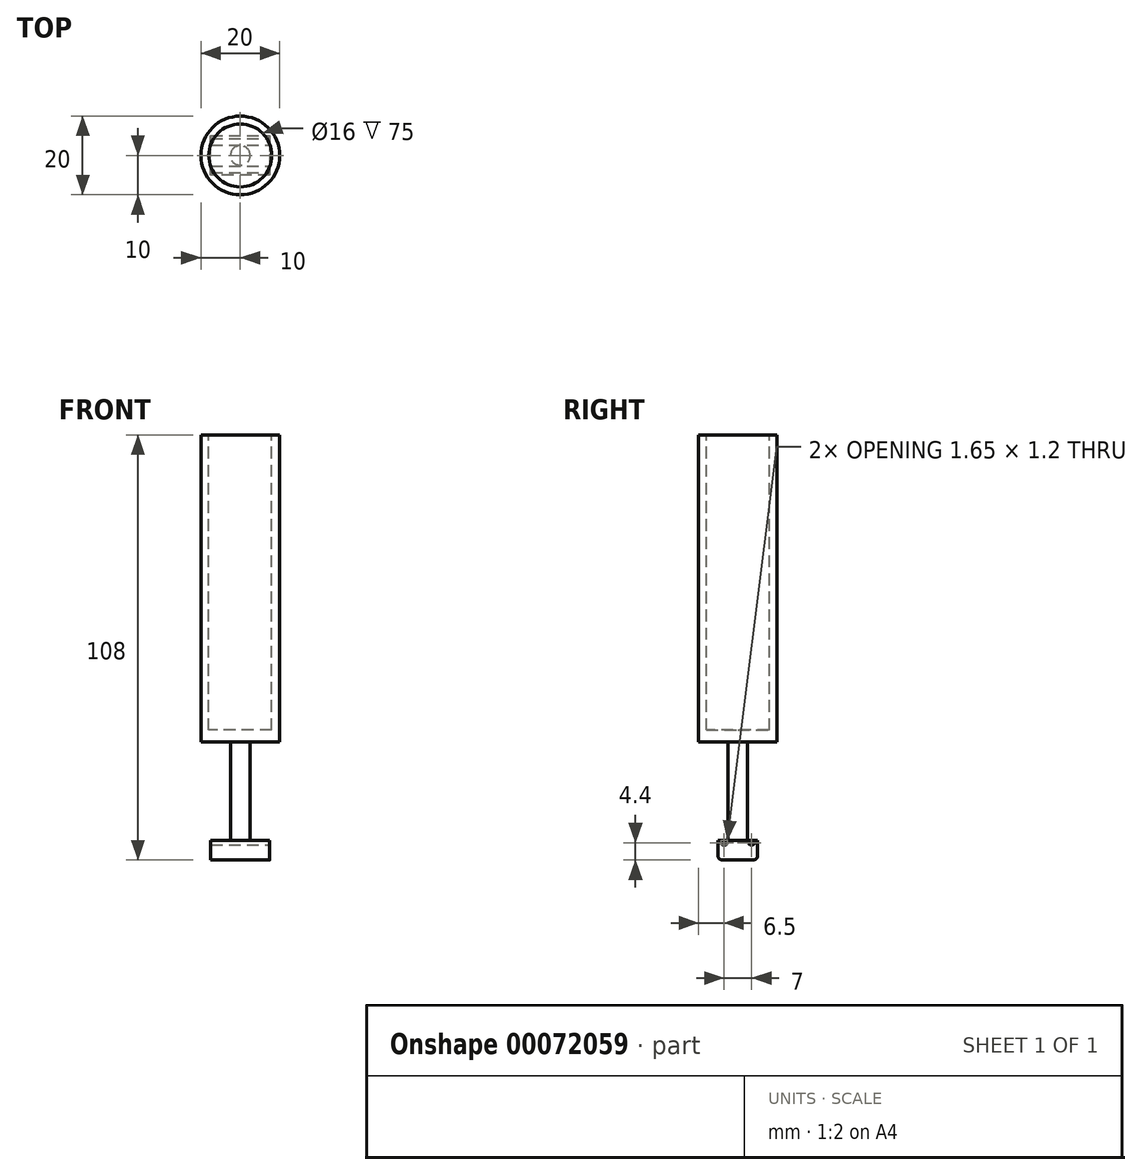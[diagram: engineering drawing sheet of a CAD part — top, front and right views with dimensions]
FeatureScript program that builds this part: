
annotation { "Feature Type Name" : "Feature", "Feature Type Description" : "" }
export const myFeature = defineFeature(function(context is Context, id is Id, definition is map)
    precondition{}
    {
        {
            var Q0;
            Q0=qCreatedBy(makeId("Top.planeOp"),FACE);
            var sketch = newSketch(context, id + "F0", { "sketchPlane" : qUnion([Q0])});
            skLineSegment(sketch, "E0", {"start": v(0, 10) * mm, "end": v(15, 10) * mm});
            skLineSegment(sketch, "E1", {"start": v(15, 10) * mm, "end": v(15, 0) * mm});
            skLineSegment(sketch, "E2", {"start": v(15, 0) * mm, "end": v(0, 0) * mm});
            skLineSegment(sketch, "E3", {"start": v(0, 0) * mm, "end": v(0, 10) * mm});
            skSolve(sketch);
        }
        {
            var Q0;
            Q0=qSketchRegion(id+"F0",true);
            extrude(context, id + "F1", {"entities" : qUnion([Q0]), "depth" : 5 * mm});
        }
        {
            var Q0;
            Q0=makeQuery(id+"F1.opExtrude","CAP_FACE",FACE,{"disambiguationData":[OSD([sQuery(id+"F0.wireOp",EDGE,"E0"),sQuery(id+"F0.wireOp",EDGE,"E1"),sQuery(id+"F0.wireOp",EDGE,"E2"),sQuery(id+"F0.wireOp",EDGE,"E3")])],"isStart":false});
            var sketch = newSketch(context, id + "F2", { "sketchPlane" : qUnion([Q0])});
            skLineSegment(sketch, "E4", {"start": v(0, 5) * mm, "end": v(15, 5) * mm, "construction": true});
            skLineSegment(sketch, "E5", {"start": v(7.5, 10) * mm, "end": v(7.5, 0) * mm, "construction": true});
            skCircle(sketch, "E6", {"center": v(7.5, 5) * mm, "radius": 2.5 * mm});
            skSolve(sketch);
        }
        {
            var Q0;
            Q0=makeQuery(id+"F2.imprint","IMPRINT",FACE,{"disambiguationData":[TD([[makeQuery(id+"F2.imprint","IMPRINT",EDGE,{"derivedFrom":sQuery(id+"F2.wireOp",EDGE,"E6")}),1.0]])]});
            var Q1;
            Q1=sQuery(id+"F2.wireOp",EDGE,"E6");
            extrude(context, id + "F3", {"entities" : qUnion([Q0]), "operationType" : NewBodyOperationType.ADD, "surfaceEntities" : qUnion([Q1]), "depth" : 100 * mm});
        }
        {
            var Q0;
            Q0=qCreatedBy(makeId("Top.planeOp"),FACE);
            cPlane(context, id + "F4", {"entities" : qUnion([Q0]), "cplaneType" : CPlaneType.OFFSET, "offset" : 30 * mm, "width" : 150 * mm, "height" : 150 * mm});
        }
        {
            var Q0;
            Q0=qCreatedBy(id+"F4.planeOp",FACE);
            var sketch = newSketch(context, id + "F5", { "sketchPlane" : qUnion([Q0])});
            skCircle(sketch, "E7", {"center": v(7.5, 5) * mm, "radius": 10 * mm});
            skSolve(sketch);
        }
        {
            var Q0;
            Q0=makeQuery(id+"F1.opExtrude","CAP_EDGE",EDGE,{"disambiguationData":[OSD([sQuery(id+"F0.wireOp",EDGE,"E2")])],"isStart":true});
            var Q1;
            Q1=makeQuery(id+"F1.opExtrude","CAP_EDGE",EDGE,{"disambiguationData":[OSD([sQuery(id+"F0.wireOp",EDGE,"E0")])],"isStart":true});
            fillet(context, id + "F6", {"entities" : qUnion([Q0, Q1]), "radius" : 1 * mm, "tangentPropagation" : true, "allowEdgeOverflow" : false});
        }
        {
            var Q0;
            Q0=makeQuery(id+"F1.opExtrude","SWEPT_FACE",FACE,{"disambiguationData":[OSD([sQuery(id+"F0.wireOp",EDGE,"E1")])]});
            var sketch = newSketch(context, id + "F7", { "sketchPlane" : qUnion([Q0])});
            skEllipse(sketch, "E8", {"center": v(1.5, 4.4) * mm, "majorRadius": 0.82 * mm, "minorRadius": 0.6 * mm, "majorAxis": v(1, 0)});
            skLineSegment(sketch, "E9", {"start": v(5, 5) * mm, "end": v(5, -1.19) * mm, "construction": true});
            skEllipse(sketch, "E10.MirrorC", {"center": v(8.5, 4.4) * mm, "majorRadius": 0.82 * mm, "minorRadius": 0.6 * mm, "majorAxis": v(-1, 0)});
            skSolve(sketch);
        }
        {
            var Q0;
            Q0=makeQuery(id+"F1.opExtrude","CAP_FACE",FACE,{"disambiguationData":[OSD([sQuery(id+"F0.wireOp",EDGE,"E0"),sQuery(id+"F0.wireOp",EDGE,"E1"),sQuery(id+"F0.wireOp",EDGE,"E2"),sQuery(id+"F0.wireOp",EDGE,"E3")])],"isStart":false});
            var sketch = newSketch(context, id + "F8", { "sketchPlane" : qUnion([Q0])});
            skCircle(sketch, "E11", {"center": v(7.5, 5) * mm, "radius": 2.5 * mm});
            skLineSegment(sketch, "E12", {"start": v(0, 5) * mm, "end": v(15, 5) * mm, "construction": true});
            skLineSegment(sketch, "E13", {"start": v(7.5, 0) * mm, "end": v(7.5, 10) * mm, "construction": true});
            skSolve(sketch);
        }
        {
            var Q0;
            {var subQ0=sQuery(id+"F7.wireOp",EDGE,"E8");var subQ1=makeQuery(id+"F1.opExtrude","CAP_EDGE",EDGE,{"disambiguationData":[OSD([sQuery(id+"F0.wireOp",EDGE,"E1")])],"isStart":false});var subQ2=makeQuery(id+"F7.imprint","INTERSECT",VERTEX,{"disambiguationData":[OD(0.0)],"derivedFrom":[subQ1,subQ0]});Q0=makeQuery(id+"F7.imprint","IMPRINT",FACE,{"disambiguationData":[TD([[makeQuery(id+"F7.imprint","IMPRINT",EDGE,{"disambiguationData":[TD([[subQ2,-1.0]])],"derivedFrom":subQ0}),1.0]])]});}
            var Q1;
            {var subQ0=sQuery(id+"F7.wireOp",EDGE,"E10.MirrorC");var subQ1=makeQuery(id+"F1.opExtrude","CAP_EDGE",EDGE,{"disambiguationData":[OSD([sQuery(id+"F0.wireOp",EDGE,"E1")])],"isStart":false});var subQ2=makeQuery(id+"F7.imprint","INTERSECT",VERTEX,{"disambiguationData":[OD(0.0)],"derivedFrom":[subQ1,subQ0]});Q1=makeQuery(id+"F7.imprint","IMPRINT",FACE,{"disambiguationData":[TD([[makeQuery(id+"F7.imprint","IMPRINT",EDGE,{"disambiguationData":[TD([[subQ2,1.0]])],"derivedFrom":subQ0}),1.0]])]});}
            extrude(context, id + "F9", {"entities" : qUnion([Q0, Q1]), "operationType" : NewBodyOperationType.REMOVE, "endBound" : BoundingType.THROUGH_ALL, "oppositeDirection" : true, "depth" : 25 * mm});
        }
        {
            var Q0;
            Q0 = qSketchRegion(id + "F5", true);
            var Q1;
            Q1=makeQuery(id+"F3.opExtrude","CAP_FACE",FACE,{"disambiguationData":[OSD([sQuery(id+"F2.wireOp",EDGE,"E6")])],"isStart":false});
            extrude(context, id + "F10", {"entities" : qUnion([Q0]), "operationType" : NewBodyOperationType.ADD, "endBound" : BoundingType.UP_TO_SURFACE, "endBoundEntityFace" : qUnion([Q1]), "depth" : 25 * mm});
        }
        {
            var Q0;
            {var subQ0=sQuery(id+"F2.wireOp",EDGE,"E6");Q0=makeQuery(id+"F10.boolean.opBoolean","MERGE",FACE,{"derivedFrom":[makeQuery(id+"F3.opExtrude","CAP_FACE",FACE,{"disambiguationData":[OSD([subQ0])],"isStart":false}),makeQuery(id+"F10.opExtrude","CAP_FACE",FACE,{"disambiguationData":[OSD([subQ0])],"isStart":false})]});}
            var sketch = newSketch(context, id + "F11", { "sketchPlane" : qUnion([Q0])});
            skCircle(sketch, "E14", {"center": v(7.5, 5) * mm, "radius": 8 * mm});
            skSolve(sketch);
        }
        {
            var Q0;
            Q0=makeQuery(id+"F11.imprint","IMPRINT",FACE,{"disambiguationData":[TD([[makeQuery(id+"F11.imprint","IMPRINT",EDGE,{"derivedFrom":sQuery(id+"F11.wireOp",EDGE,"E14")}),1.0]])]});
            extrude(context, id + "F12", {"entities" : qUnion([Q0]), "operationType" : NewBodyOperationType.REMOVE, "oppositeDirection" : true, "depth" : 72 * mm});
        }
        {
            var Q0;
            {var subQ0=sQuery(id+"F2.wireOp",EDGE,"E6");Q0=makeQuery(id+"F10.boolean.opBoolean","MERGE",FACE,{"derivedFrom":[makeQuery(id+"F3.opExtrude","CAP_FACE",FACE,{"disambiguationData":[OSD([subQ0])],"isStart":false}),makeQuery(id+"F10.opExtrude","CAP_FACE",FACE,{"disambiguationData":[OSD([subQ0])],"isStart":false})]});}
            var sketch = newSketch(context, id + "F13", { "sketchPlane" : qUnion([Q0])});
            skCircle(sketch, "E15", {"center": v(7.5, 5) * mm, "radius": 10 * mm});
            skSolve(sketch);
        }
        {
            var Q0;
            Q0=makeQuery(id+"F13.imprint","IMPRINT",FACE,{"disambiguationData":[TD([[makeQuery(id+"F13.imprint","IMPRINT",EDGE,{"derivedFrom":sQuery(id+"F13.wireOp",EDGE,"E15")}),1.0]])]});
            var sketch = newSketch(context, id + "F14", { "sketchPlane" : qUnion([Q0])});
            skPoint(sketch, "E16.0", {"position": v(7.5, 5) * mm});
            skCircle(sketch, "E17", {"center": v(7.5, 5) * mm, "radius": 10 * mm});
            skSolve(sketch);
        }
        {
            var Q0;
            Q0=makeQuery(id+"F13.imprint","IMPRINT",FACE,{"disambiguationData":[TD([[makeQuery(id+"F13.imprint","IMPRINT",EDGE,{"derivedFrom":makeQuery(id+"F12.boolean.opBoolean","COPY",EDGE,{"derivedFrom":makeQuery(id+"F12.opExtrude","CAP_EDGE",EDGE,{"disambiguationData":[OSD([sQuery(id+"F11.wireOp",EDGE,"E14")])],"isStart":true})})}),1.0]])]});
            var Q1;
            Q1=makeQuery(id+"F13.imprint","IMPRINT",FACE,{"disambiguationData":[TD([[makeQuery(id+"F13.imprint","IMPRINT",EDGE,{"derivedFrom":sQuery(id+"F13.wireOp",EDGE,"E15")}),1.0]])]});
            var Q2;
            Q2=sQuery(id+"F14.wireOp",EDGE,"E17");
            extrude(context, id + "F15", {"entities" : qUnion([Q0, Q1]), "operationType" : NewBodyOperationType.ADD, "surfaceEntities" : qUnion([Q2]), "depth" : 3 * mm});
        }
    });
